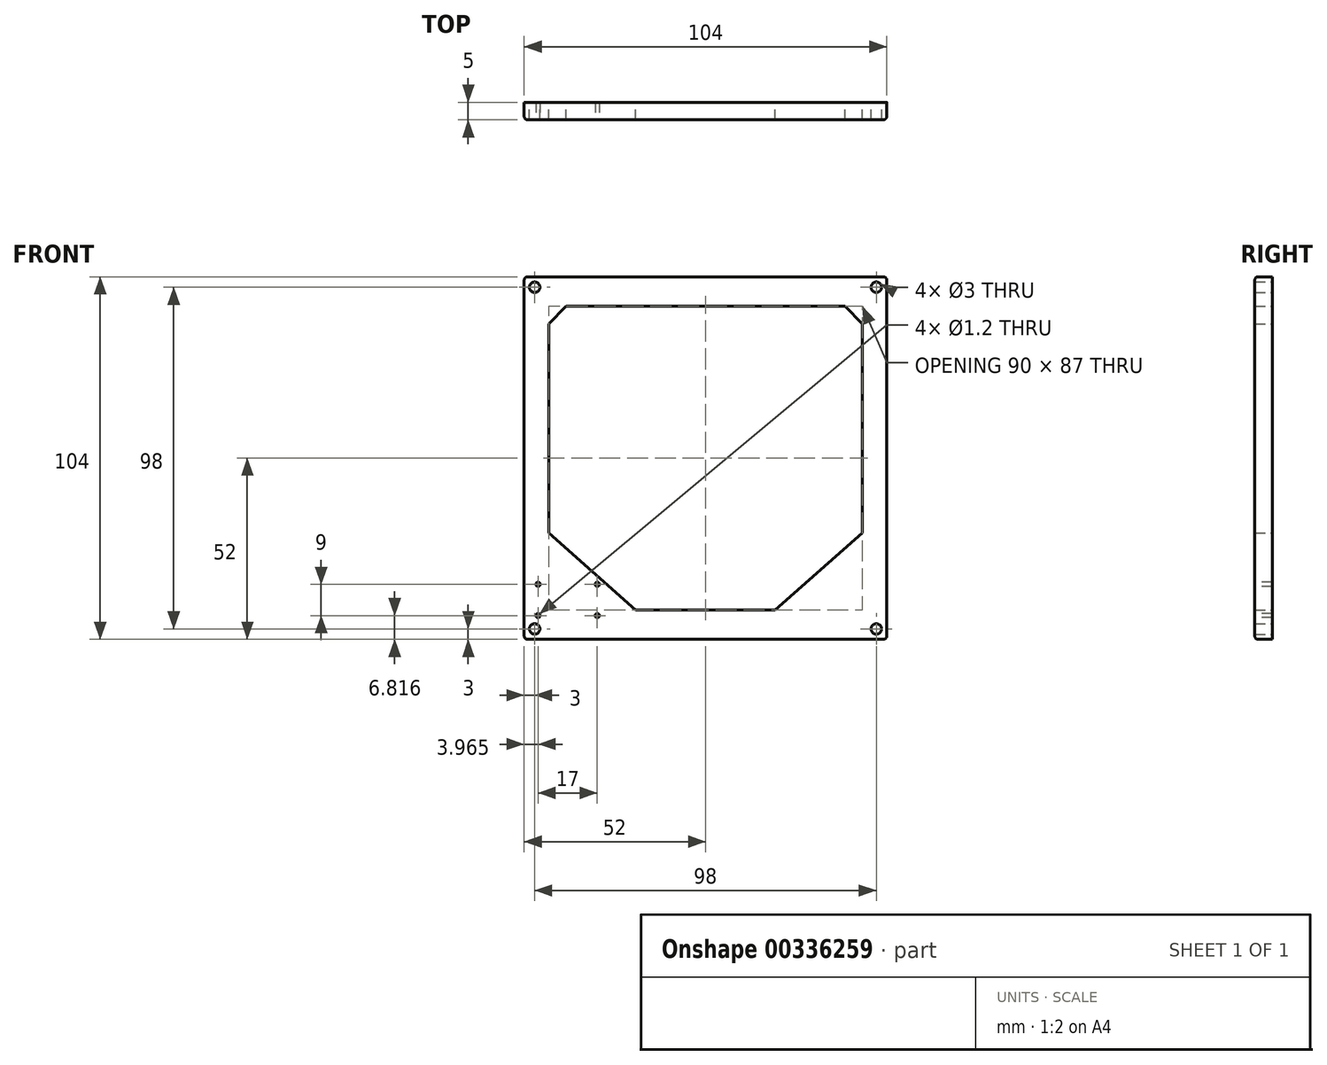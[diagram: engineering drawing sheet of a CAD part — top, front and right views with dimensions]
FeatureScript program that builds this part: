
annotation { "Feature Type Name" : "Feature", "Feature Type Description" : "" }
export const myFeature = defineFeature(function(context is Context, id is Id, definition is map)
    precondition{}
    {
        {
            var Q0;
            Q0=qCreatedBy(makeId("Front.planeOp"),FACE);
            var sketch = newSketch(context, id + "F0", { "sketchPlane" : qUnion([Q0])});
            skLineSegment(sketch, "E0.bottom", {"start": v(-52, 52) * mm, "end": v(52, 52) * mm});
            skLineSegment(sketch, "E0.top", {"start": v(-52, -52) * mm, "end": v(52, -52) * mm});
            skLineSegment(sketch, "E0.left", {"start": v(-52, 52) * mm, "end": v(-52, -52) * mm});
            skLineSegment(sketch, "E0.right", {"start": v(52, 52) * mm, "end": v(52, -52) * mm});
            skCircle(sketch, "E1", {"center": v(-49, 49) * mm, "radius": 1.5 * mm});
            skCircle(sketch, "E2", {"center": v(49, 49) * mm, "radius": 1.5 * mm});
            skCircle(sketch, "E3", {"center": v(-49, -49) * mm, "radius": 1.5 * mm});
            skCircle(sketch, "E4", {"center": v(49, -49) * mm, "radius": 1.5 * mm});
            skCircle(sketch, "E5", {"center": v(-41, -41) * mm, "radius": 2.5 * mm, "construction": true});
            skCircle(sketch, "E6", {"center": v(41, -41) * mm, "radius": 2.5 * mm, "construction": true});
            skSolve(sketch);
        }
        {
            var Q0;
            Q0=qCreatedBy(makeId("Front.planeOp"),FACE);
            var sketch = newSketch(context, id + "F1", { "sketchPlane" : qUnion([Q0])});
            skLineSegment(sketch, "E7", {"start": v(-40, 43.5) * mm, "end": v(40, 43.5) * mm});
            skLineSegment(sketch, "E8", {"start": v(40, 43.5) * mm, "end": v(45, 38.5) * mm});
            skLineSegment(sketch, "E9", {"start": v(45, 38.5) * mm, "end": v(45, -21.5) * mm});
            skLineSegment(sketch, "E10", {"start": v(45, -21.5) * mm, "end": v(20, -43.5) * mm});
            skLineSegment(sketch, "E11", {"start": v(20, -43.5) * mm, "end": v(-20, -43.5) * mm});
            skLineSegment(sketch, "E12", {"start": v(-20, -43.5) * mm, "end": v(-45, -21.5) * mm});
            skLineSegment(sketch, "E13", {"start": v(-45, -21.5) * mm, "end": v(-45, 38.5) * mm});
            skLineSegment(sketch, "E14", {"start": v(-45, 38.5) * mm, "end": v(-40, 43.5) * mm});
            skSolve(sketch);
        }
        {
            var Q0;
            Q0=makeQuery(id+"F0.imprint","IMPRINT",FACE,{"disambiguationData":[TD([[makeQuery(id+"F0.imprint","IMPRINT",EDGE,{"derivedFrom":sQuery(id+"F0.wireOp",EDGE,"E0.bottom")}),-1.0]])]});
            extrude(context, id + "F2", {"entities" : qUnion([Q0]), "depth" : 5 * mm});
        }
        {
            var Q0;
            Q0=qSketchRegion(id+"F1",true);
            var Q1;
            Q1=makeQuery(id+"F2.opExtrude","CAP_FACE",FACE,{"disambiguationData":[OSD([sQuery(id+"F0.wireOp",EDGE,"E0.bottom"),sQuery(id+"F0.wireOp",EDGE,"E0.top"),sQuery(id+"F0.wireOp",EDGE,"E0.left"),sQuery(id+"F0.wireOp",EDGE,"E0.right"),sQuery(id+"F0.wireOp",EDGE,"E1"),sQuery(id+"F0.wireOp",EDGE,"E2"),sQuery(id+"F0.wireOp",EDGE,"E3"),sQuery(id+"F0.wireOp",EDGE,"E4")])],"isStart":false});
            extrude(context, id + "F3", {"entities" : qUnion([Q0, Q1]), "operationType" : NewBodyOperationType.REMOVE, "depth" : 25 * mm});
        }
        {
            var Q0;
            Q0=makeQuery(id+"F2.opExtrude","SWEPT_EDGE",EDGE,{"disambiguationData":[OSD([sQuery(id+"F0.wireOp",EDGE,"E0.bottom"),sQuery(id+"F0.wireOp",EDGE,"E0.left")])]});
            var Q1;
            Q1=makeQuery(id+"F2.opExtrude","CAP_EDGE",EDGE,{"disambiguationData":[OSD([sQuery(id+"F0.wireOp",EDGE,"E0.left")])],"isStart":false});
            var Q2;
            Q2=makeQuery(id+"F2.opExtrude","CAP_EDGE",EDGE,{"disambiguationData":[OSD([sQuery(id+"F0.wireOp",EDGE,"E0.bottom")])],"isStart":false});
            var Q3;
            Q3=makeQuery(id+"F2.opExtrude","SWEPT_EDGE",EDGE,{"disambiguationData":[OSD([sQuery(id+"F0.wireOp",EDGE,"E0.top"),sQuery(id+"F0.wireOp",EDGE,"E0.left")])]});
            var Q4;
            Q4=makeQuery(id+"F2.opExtrude","CAP_EDGE",EDGE,{"disambiguationData":[OSD([sQuery(id+"F0.wireOp",EDGE,"E0.top")])],"isStart":false});
            var Q5;
            Q5=makeQuery(id+"F2.opExtrude","CAP_EDGE",EDGE,{"disambiguationData":[OSD([sQuery(id+"F0.wireOp",EDGE,"E0.right")])],"isStart":false});
            var Q6;
            Q6=makeQuery(id+"F2.opExtrude","SWEPT_EDGE",EDGE,{"disambiguationData":[OSD([sQuery(id+"F0.wireOp",EDGE,"E0.bottom"),sQuery(id+"F0.wireOp",EDGE,"E0.right")])]});
            var Q7;
            Q7=makeQuery(id+"F2.opExtrude","SWEPT_EDGE",EDGE,{"disambiguationData":[OSD([sQuery(id+"F0.wireOp",EDGE,"E0.top"),sQuery(id+"F0.wireOp",EDGE,"E0.right")])]});
            fillet(context, id + "F4", {"entities" : qUnion([Q0, Q1, Q2, Q3, Q4, Q5, Q6, Q7]), "radius" : 1 * mm, "tangentPropagation" : true, "allowEdgeOverflow" : false});
        }
        {
            var Q0;
            Q0=makeQuery(id+"F2.opExtrude","CAP_FACE",FACE,{"disambiguationData":[OSD([sQuery(id+"F0.wireOp",EDGE,"E0.bottom"),sQuery(id+"F0.wireOp",EDGE,"E0.top"),sQuery(id+"F0.wireOp",EDGE,"E0.left"),sQuery(id+"F0.wireOp",EDGE,"E0.right"),sQuery(id+"F0.wireOp",EDGE,"E1"),sQuery(id+"F0.wireOp",EDGE,"E2"),sQuery(id+"F0.wireOp",EDGE,"E3"),sQuery(id+"F0.wireOp",EDGE,"E4")])],"isStart":false});
            var sketch = newSketch(context, id + "F5", { "sketchPlane" : qUnion([Q0])});
            skCircle(sketch, "E15", {"center": v(-48.04, -36.18) * mm, "radius": 0.6 * mm});
            skCircle(sketch, "E16", {"center": v(-48.04, -45.18) * mm, "radius": 0.6 * mm});
            skCircle(sketch, "E17", {"center": v(-31.04, -36.18) * mm, "radius": 0.6 * mm});
            skCircle(sketch, "E18", {"center": v(-31.04, -45.18) * mm, "radius": 0.6 * mm});
            skSolve(sketch);
        }
        {
            var Q0;
            Q0 = qSketchRegion(id + "F5", true);
            extrude(context, id + "F6", {"entities" : qUnion([Q0]), "operationType" : NewBodyOperationType.REMOVE, "oppositeDirection" : true, "depth" : 25 * mm});
        }
    });
